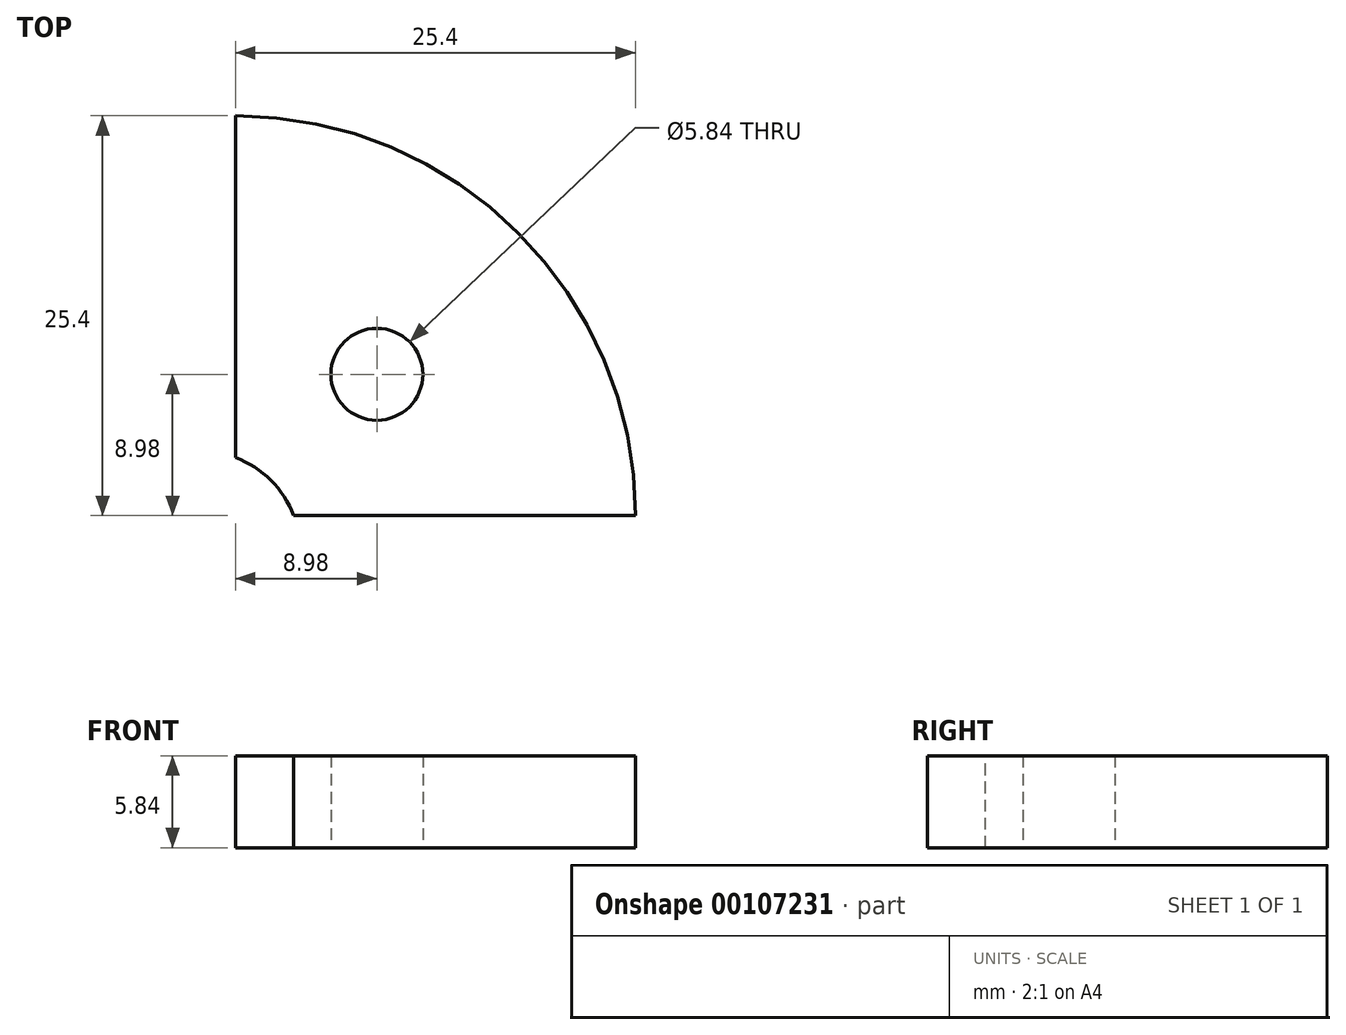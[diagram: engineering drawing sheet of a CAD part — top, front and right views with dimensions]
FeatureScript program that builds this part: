
annotation { "Feature Type Name" : "Feature", "Feature Type Description" : "" }
export const myFeature = defineFeature(function(context is Context, id is Id, definition is map)
    precondition{}
    {
        {
            var Q0;
            Q0=qCreatedBy(makeId("Top.planeOp"),FACE);
            var sketch = newSketch(context, id + "F0", { "sketchPlane" : qUnion([Q0])});
            skLineSegment(sketch, "E0", {"start": v(0, 0) * mm, "end": v(0, 25.4) * mm});
            skLineSegment(sketch, "E1", {"start": v(0, 0) * mm, "end": v(25.4, 0) * mm});
            skArc(sketch, "E2", {"start": v(25.4, 0) * mm, "mid": v(17.96, 17.96) * mm, "end": v(0, 25.4) * mm});
            skLineSegment(sketch, "E3", {"start": v(0, 0) * mm, "end": v(8.98, 8.98) * mm, "construction": true});
            skCircle(sketch, "E4", {"center": v(8.98, 8.98) * mm, "radius": 2.92 * mm});
            skSolve(sketch);
        }
        {
            var Q0;
            Q0=makeQuery(id+"F0.imprint","IMPRINT",FACE,{"disambiguationData":[TD([[makeQuery(id+"F0.imprint","IMPRINT",EDGE,{"derivedFrom":sQuery(id+"F0.wireOp",EDGE,"E0")}),-1.0]])]});
            extrude(context, id + "F1", {"entities" : qUnion([Q0]), "depth" : 5.84 * mm});
        }
        {
            var Q0;
            Q0=makeQuery(id+"F1.opExtrude","CAP_FACE",FACE,{"disambiguationData":[OSD([sQuery(id+"F0.wireOp",EDGE,"E0"),sQuery(id+"F0.wireOp",EDGE,"E1"),sQuery(id+"F0.wireOp",EDGE,"E2"),sQuery(id+"F0.wireOp",EDGE,"E4")])],"isStart":false});
            var sketch = newSketch(context, id + "F2", { "sketchPlane" : qUnion([Q0])});
            skCircle(sketch, "E5", {"center": v(-2.25, -2.25) * mm, "radius": 6.35 * mm});
            skLineSegment(sketch, "E6", {"start": v(0, 0) * mm, "end": v(-2.25, -2.25) * mm, "construction": true});
            skSolve(sketch);
        }
        {
            var Q0;
            {var subQ0=sQuery(id+"F2.wireOp",EDGE,"E5");var subQ1=makeQuery(id+"F1.opExtrude","CAP_EDGE",EDGE,{"disambiguationData":[OSD([sQuery(id+"F0.wireOp",EDGE,"E0")])],"isStart":false});var subQ2=makeQuery(id+"F2.imprint","INTERSECT",VERTEX,{"derivedFrom":[subQ1,subQ0]});Q0=makeQuery(id+"F2.imprint","IMPRINT",FACE,{"disambiguationData":[TD([[makeQuery(id+"F2.imprint","IMPRINT",EDGE,{"disambiguationData":[TD([[subQ2,1.0]])],"derivedFrom":subQ0}),1.0]])]});}
            var Q1;
            Q1=makeQuery(id+"F1.opExtrude","CAP_FACE",FACE,{"disambiguationData":[OSD([sQuery(id+"F0.wireOp",EDGE,"E0"),sQuery(id+"F0.wireOp",EDGE,"E1"),sQuery(id+"F0.wireOp",EDGE,"E2"),sQuery(id+"F0.wireOp",EDGE,"E4")])],"isStart":true});
            extrude(context, id + "F3", {"entities" : qUnion([Q0]), "operationType" : NewBodyOperationType.REMOVE, "endBound" : BoundingType.UP_TO_SURFACE, "oppositeDirection" : true, "endBoundEntityFace" : qUnion([Q1]), "depth" : 25.4 * mm});
        }
    });
